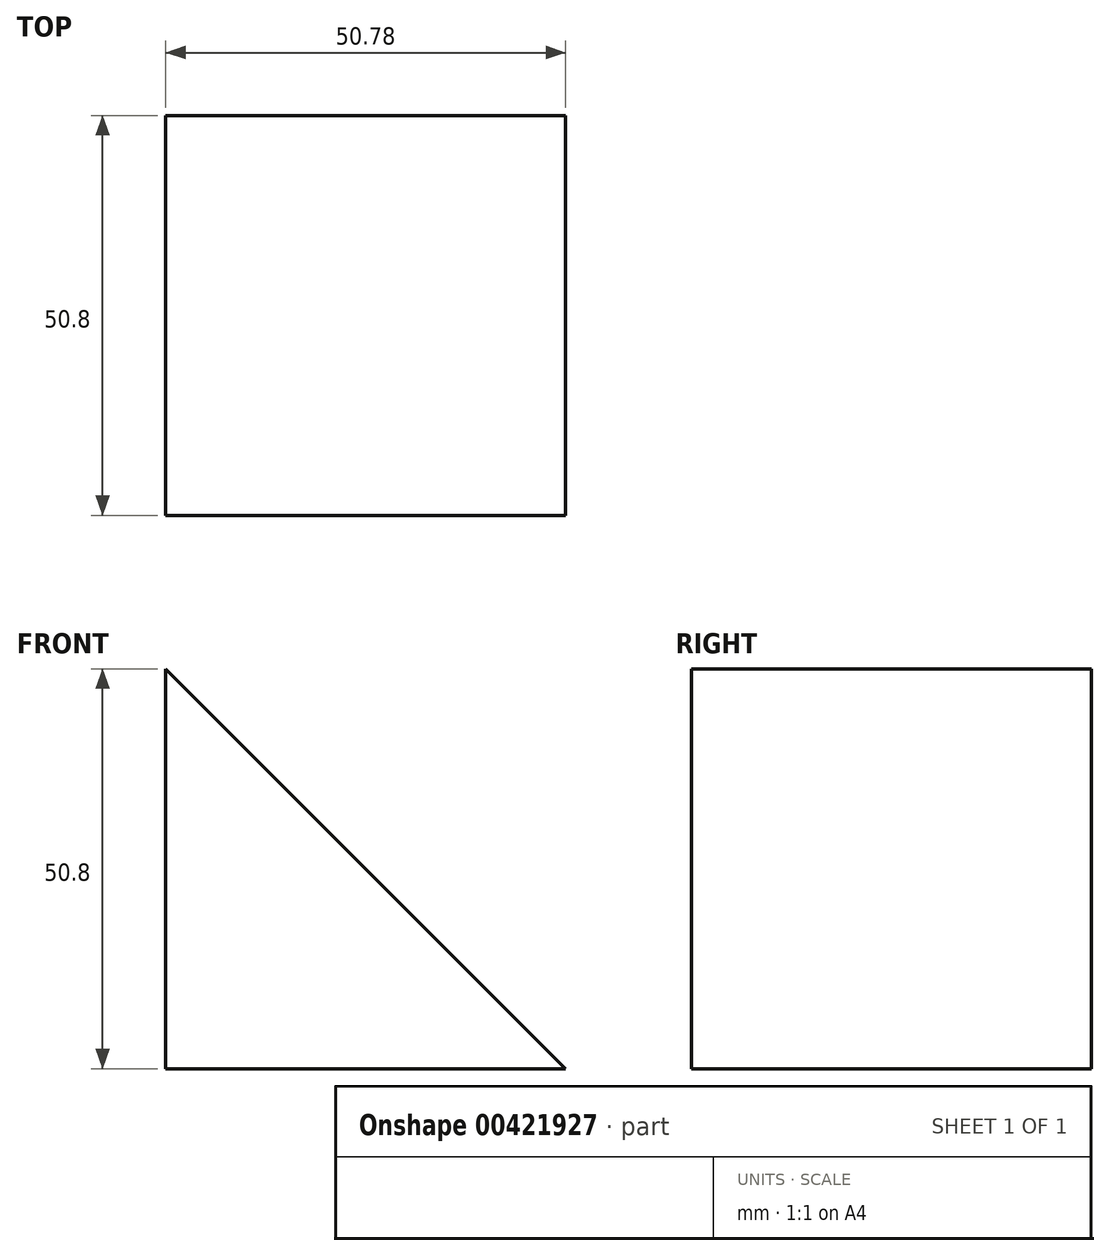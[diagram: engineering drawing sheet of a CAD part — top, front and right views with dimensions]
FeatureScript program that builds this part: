
annotation { "Feature Type Name" : "Feature", "Feature Type Description" : "" }
export const myFeature = defineFeature(function(context is Context, id is Id, definition is map)
    precondition{}
    {
        {
            var Q0;
            Q0=qCreatedBy(makeId("Front.planeOp"),FACE);
            var sketch = newSketch(context, id + "F0", { "sketchPlane" : qUnion([Q0])});
            skLineSegment(sketch, "E0", {"start": v(0, 0) * mm, "end": v(-50.78, 0) * mm});
            skLineSegment(sketch, "E1", {"start": v(-50.78, 0) * mm, "end": v(-50.78, 50.8) * mm});
            skLineSegment(sketch, "E2", {"start": v(-50.78, 50.8) * mm, "end": v(0, 0) * mm});
            skSolve(sketch);
        }
        {
            var Q0;
            Q0 = qSketchRegion(id + "F0", true);
            extrude(context, id + "F1", {"entities" : qUnion([Q0]), "depth" : 50.8 * mm});
        }
    });
